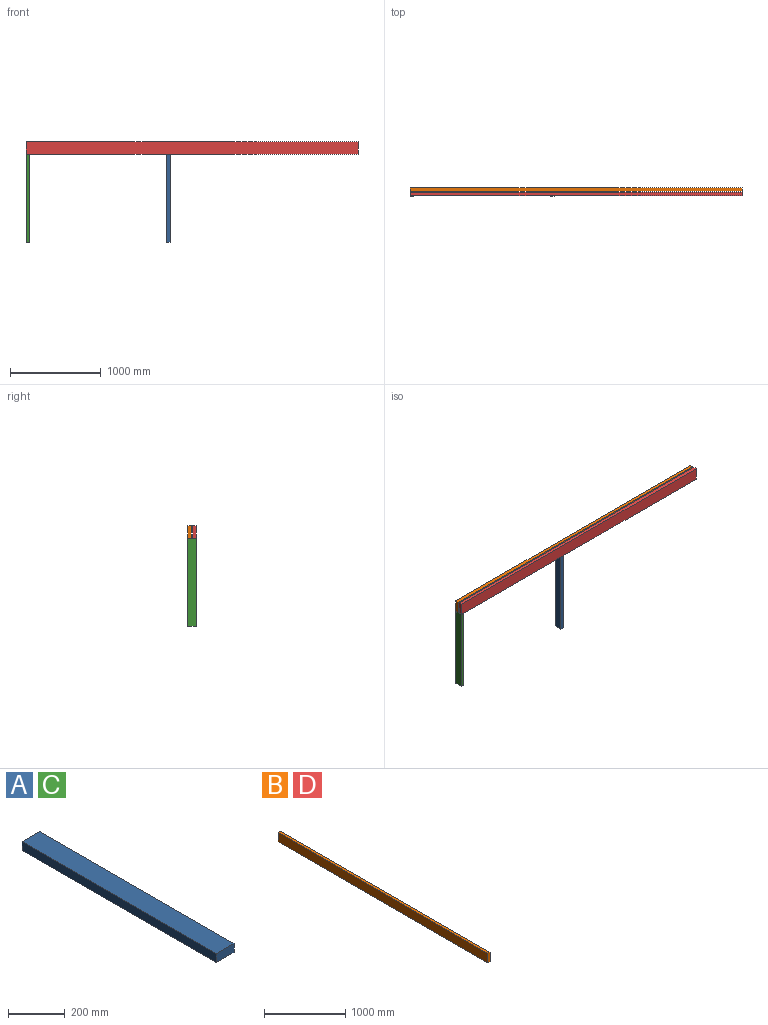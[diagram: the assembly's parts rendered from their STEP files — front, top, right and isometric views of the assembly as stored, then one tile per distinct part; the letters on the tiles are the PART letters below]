
ASSEMBLY  parts=4 mates=1
PART A: 6 faces, bbox 88.9x971.6x38.1 mm
  f0: plane 971.55x88.9mm, normal (0,0,1), area 86370.8mm2, adj f1,f3,f4,f5
  f1: plane 971.55x38.1mm, normal (-1,0,0), area 37016.1mm2, adj f0,f2,f4,f5
  f2: plane 971.55x88.9mm, normal (0,0,-1), area 86370.8mm2, adj f1,f3,f4,f5
  f3: plane 971.55x38.1mm, normal (1,0,0), area 37016.1mm2, adj f0,f2,f4,f5
  f4: plane 88.9x38.1mm, normal (0,-1,0), area 3387.1mm2, adj f0,f1,f2,f3
  f5: plane 88.9x38.1mm, normal (0,1,0), area 3387.1mm2, adj f0,f1,f2,f3
PART B: 6 faces, bbox 38.1x3657.6x139.7 mm
  f0: plane 3657.6x38.1mm, normal (0,0,-1), area 139354.6mm2, adj f1,f3,f4,f5
  f1: plane 3657.6x139.7mm, normal (1,0,0), area 510966.7mm2, adj f0,f2,f4,f5
  f2: plane 3657.6x38.1mm, normal (0,0,1), area 139354.6mm2, adj f1,f3,f4,f5
  f3: plane 3657.6x139.7mm, normal (-1,0,0), area 510966.7mm2, adj f0,f2,f4,f5
  f4: plane 139.7x38.1mm, normal (0,-1,0), area 5322.6mm2, adj f0,f1,f2,f3
  f5: plane 139.7x38.1mm, normal (0,1,0), area 5322.6mm2, adj f0,f1,f2,f3
PART C: same geometry as A
PART D: same geometry as B
PLACE A rot(axis=(-0.58,0.58,-0.58),120deg) t=(-1379.09,1445.9,-1353.3)mm
PLACE B rot(axis=(0,0,-1),90deg) t=(710.06,-188.34,-311.9)mm
PLACE C rot(axis=(-0.58,0.58,-0.58),120deg) t=(-2928.49,1445.9,-1353.3)mm
PLACE D rot(axis=(0,0,-1),90deg) t=(710.06,-239.14,-311.9)mm fixed
MATE fastened C.f4 <-> D.f0  axis (0,0,1) through (-2947.54,-442.34,-381.75)mm
